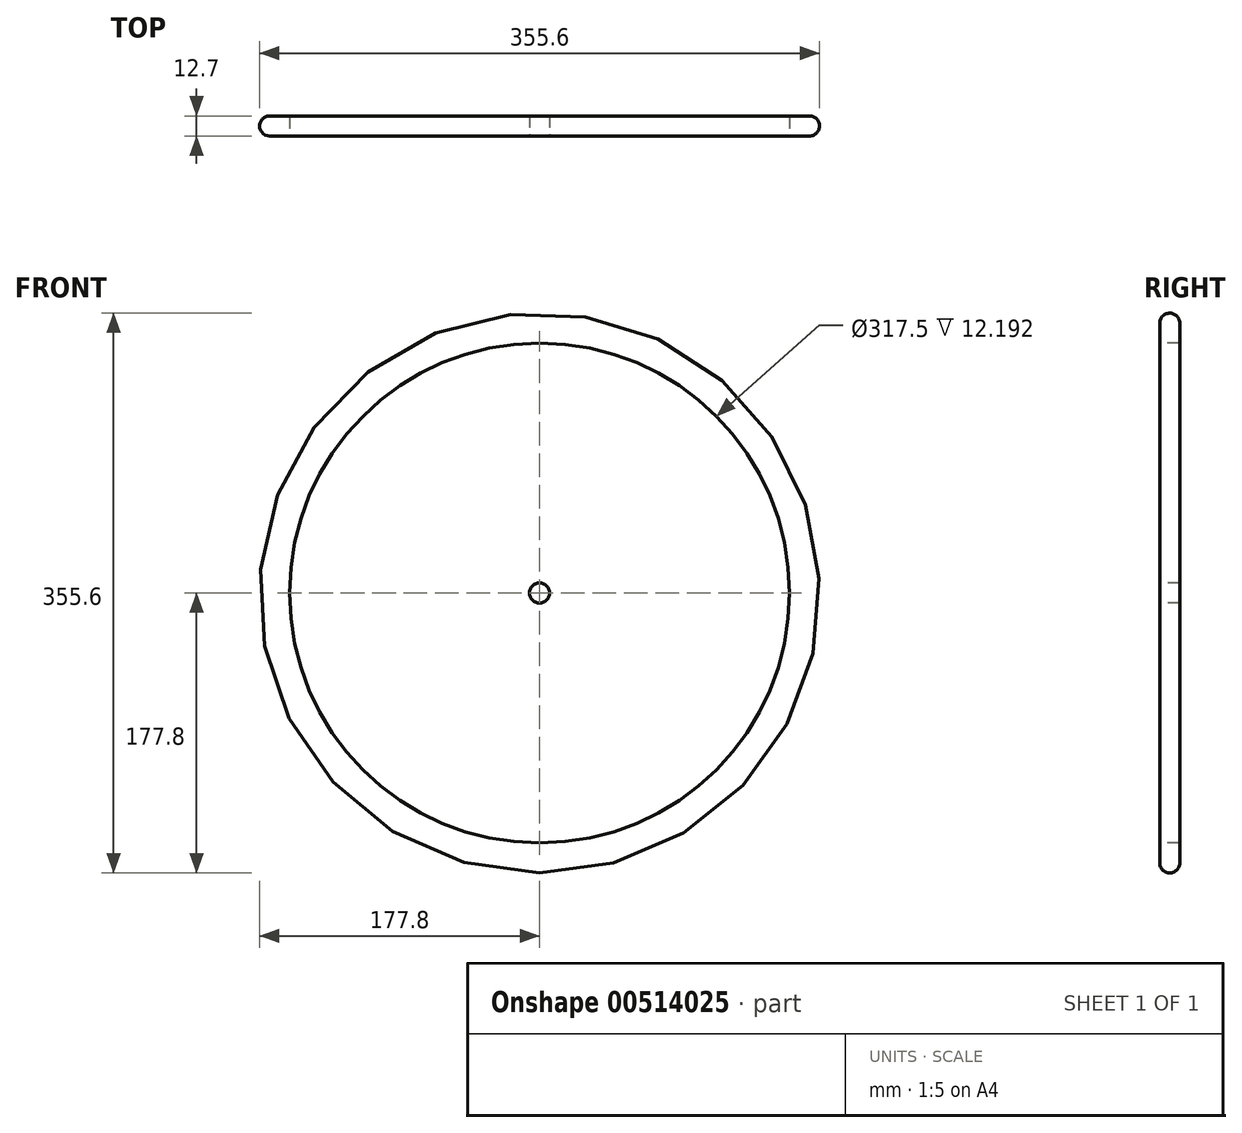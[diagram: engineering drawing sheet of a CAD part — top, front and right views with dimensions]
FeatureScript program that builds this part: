
annotation { "Feature Type Name" : "Feature", "Feature Type Description" : "" }
export const myFeature = defineFeature(function(context is Context, id is Id, definition is map)
    precondition{}
    {
        {
            var Q0;
            Q0=qCreatedBy(makeId("Front.planeOp"),FACE);
            var sketch = newSketch(context, id + "F0", { "sketchPlane" : qUnion([Q0])});
            skCircle(sketch, "E0", {"center": v(0, 0) * mm, "radius": 177.8 * mm});
            skSolve(sketch);
        }
        {
            var Q0;
            Q0=makeQuery(id+"F0.imprint","IMPRINT",FACE,{"disambiguationData":[TD([[makeQuery(id+"F0.imprint","IMPRINT",EDGE,{"derivedFrom":sQuery(id+"F0.wireOp",EDGE,"E0")}),1.0]])]});
            extrude(context, id + "F1", {"entities" : qUnion([Q0]), "depth" : 12.7 * mm, "offsetDistance" : 25.4 * mm});
        }
        {
            var Q0;
            Q0=makeQuery(id+"F1.opExtrude","CAP_FACE",FACE,{"disambiguationData":[OSD([sQuery(id+"F0.wireOp",EDGE,"E0")])],"isStart":false});
            var sketch = newSketch(context, id + "F2", { "sketchPlane" : qUnion([Q0])});
            skCircle(sketch, "E1", {"center": v(0, 0) * mm, "radius": 158.75 * mm});
            skCircle(sketch, "E2", {"center": v(0, 0) * mm, "radius": 6.35 * mm});
            skSolve(sketch);
        }
        {
            var Q0;
            Q0=makeQuery(id+"F2.imprint","IMPRINT",FACE,{"disambiguationData":[TD([[makeQuery(id+"F2.imprint","IMPRINT",EDGE,{"derivedFrom":sQuery(id+"F2.wireOp",EDGE,"E1")}),1.0]])]});
            extrude(context, id + "F3", {"entities" : qUnion([Q0]), "operationType" : NewBodyOperationType.REMOVE, "endBound" : BoundingType.THROUGH_ALL, "oppositeDirection" : true, "depth" : 25.4 * mm, "offsetDistance" : 25.4 * mm});
        }
        {
            var Q0;
            Q0=makeQuery(id+"F1.opExtrude","CAP_EDGE",EDGE,{"disambiguationData":[OSD([sQuery(id+"F0.wireOp",EDGE,"E0")])],"isStart":false});
            var Q1;
            Q1=makeQuery(id+"F1.opExtrude","CAP_EDGE",EDGE,{"disambiguationData":[OSD([sQuery(id+"F0.wireOp",EDGE,"E0")])],"isStart":true});
            fillet(context, id + "F4", {"entities" : qUnion([Q0, Q1]), "radius" : 6.35 * mm, "tangentPropagation" : true, "allowEdgeOverflow" : false});
        }
        {
            var Q0;
            Q0=makeQuery(id+"F3.boolean.opBoolean","INTERSECT",EDGE,{"derivedFrom":[makeQuery(id+"F1.opExtrude","CAP_FACE",FACE,{"disambiguationData":[OSD([sQuery(id+"F0.wireOp",EDGE,"E0")])],"isStart":true}),makeQuery(id+"F3.opExtrude","SWEPT_FACE",FACE,{"disambiguationData":[OSD([sQuery(id+"F2.wireOp",EDGE,"E1")])]})]});
            var Q1;
            Q1=makeQuery(id+"F3.boolean.opBoolean","COPY",EDGE,{"derivedFrom":makeQuery(id+"F3.opExtrude","CAP_EDGE",EDGE,{"disambiguationData":[OSD([sQuery(id+"F2.wireOp",EDGE,"E1")])],"isStart":true})});
            fillet(context, id + "F5", {"entities" : qUnion([Q0, Q1]), "radius" : 0.5 * mm, "tangentPropagation" : true, "allowEdgeOverflow" : false});
        }
    });
